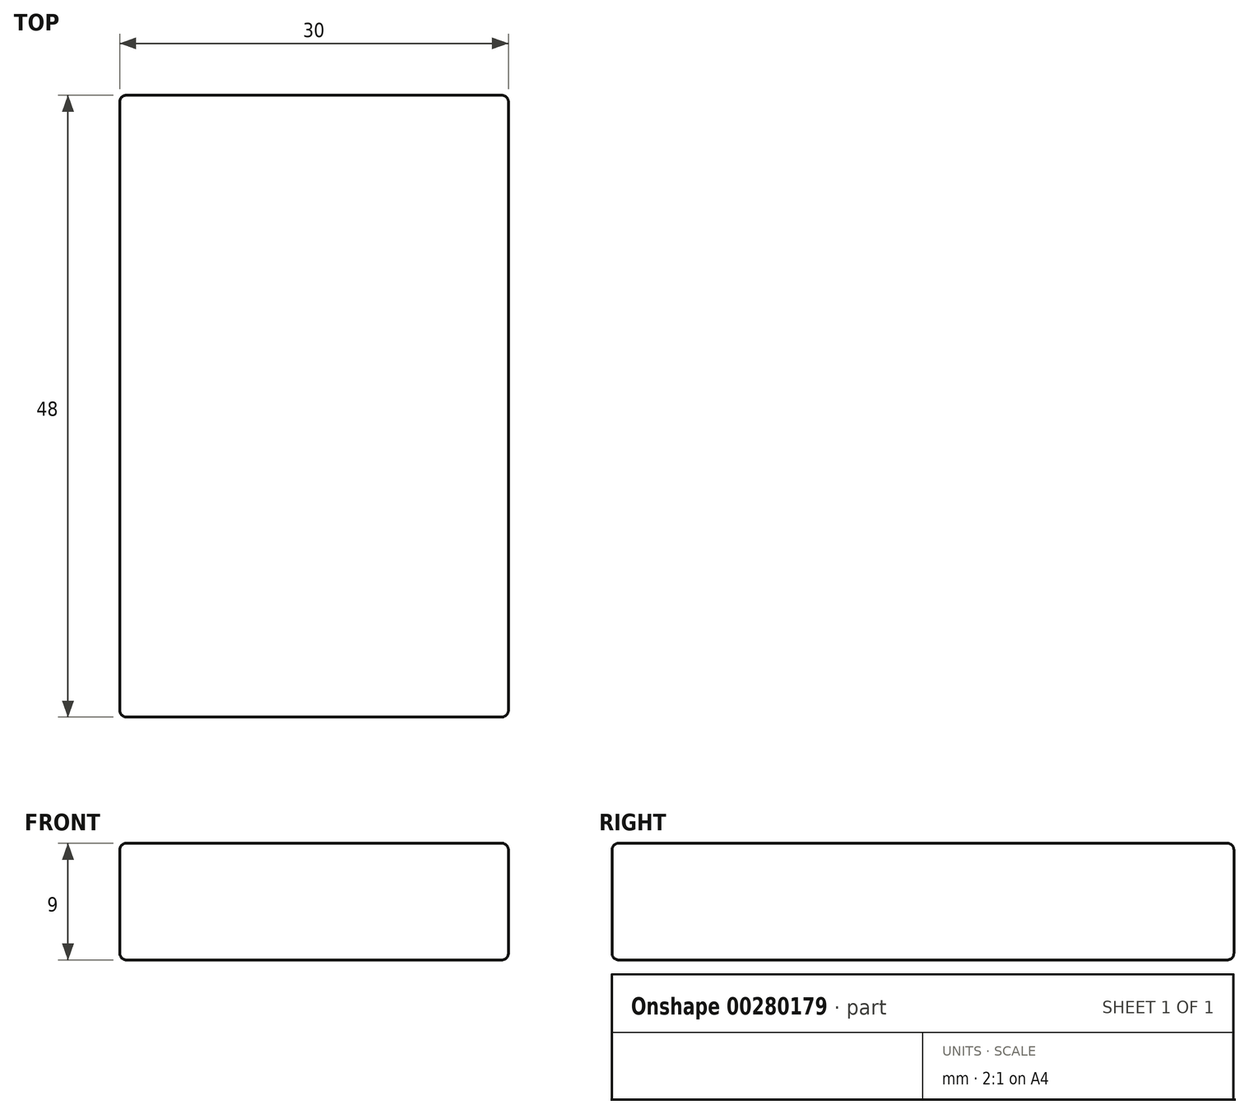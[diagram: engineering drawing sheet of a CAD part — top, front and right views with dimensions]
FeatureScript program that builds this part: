
annotation { "Feature Type Name" : "Feature", "Feature Type Description" : "" }
export const myFeature = defineFeature(function(context is Context, id is Id, definition is map)
    precondition{}
    {
        {
            var Q0;
            Q0=qCreatedBy(makeId("Front.planeOp"),FACE);
            var sketch = newSketch(context, id + "F0", { "sketchPlane" : qUnion([Q0])});
            skLineSegment(sketch, "E0.bottom", {"start": v(15, -4.5) * mm, "end": v(-15, -4.5) * mm});
            skLineSegment(sketch, "E0.top", {"start": v(15, 4.5) * mm, "end": v(-15, 4.5) * mm});
            skLineSegment(sketch, "E0.left", {"start": v(15, -4.5) * mm, "end": v(15, 4.5) * mm});
            skLineSegment(sketch, "E0.right", {"start": v(-15, -4.5) * mm, "end": v(-15, 4.5) * mm});
            skPoint(sketch, "E0.middle", {"position": v(0, 0) * mm});
            skSolve(sketch);
        }
        {
            var Q0;
            Q0 = qSketchRegion(id + "F0", true);
            extrude(context, id + "F1", {"entities" : qUnion([Q0]), "depth" : 48 * mm, "symmetric" : true});
        }
        {
            var Q0;
            Q0=makeQuery(id+"F1.opExtrude","SWEPT_EDGE",EDGE,{"disambiguationData":[OSD([sQuery(id+"F0.wireOp",EDGE,"E0.bottom"),sQuery(id+"F0.wireOp",EDGE,"E0.left")])]});
            var Q1;
            Q1=makeQuery(id+"F1.opExtrude","SWEPT_FACE",FACE,{"disambiguationData":[OSD([sQuery(id+"F0.wireOp",EDGE,"E0.bottom")])]});
            var Q2;
            Q2=makeQuery(id+"F1.opExtrude","CAP_FACE",FACE,{"disambiguationData":[OSD([sQuery(id+"F0.wireOp",EDGE,"E0.bottom"),sQuery(id+"F0.wireOp",EDGE,"E0.top"),sQuery(id+"F0.wireOp",EDGE,"E0.left"),sQuery(id+"F0.wireOp",EDGE,"E0.right")])],"isStart":true});
            var Q3;
            Q3=makeQuery(id+"F1.opExtrude","SWEPT_EDGE",EDGE,{"disambiguationData":[OSD([sQuery(id+"F0.wireOp",EDGE,"E0.top"),sQuery(id+"F0.wireOp",EDGE,"E0.left")])]});
            var Q4;
            Q4=makeQuery(id+"F1.opExtrude","CAP_FACE",FACE,{"disambiguationData":[OSD([sQuery(id+"F0.wireOp",EDGE,"E0.bottom"),sQuery(id+"F0.wireOp",EDGE,"E0.top"),sQuery(id+"F0.wireOp",EDGE,"E0.left"),sQuery(id+"F0.wireOp",EDGE,"E0.right")])],"isStart":false});
            var Q5;
            Q5=makeQuery(id+"F1.opExtrude","SWEPT_EDGE",EDGE,{"disambiguationData":[OSD([sQuery(id+"F0.wireOp",EDGE,"E0.top"),sQuery(id+"F0.wireOp",EDGE,"E0.right")])]});
            var Q6;
            Q6=makeQuery(id+"F1.opExtrude","SWEPT_FACE",FACE,{"disambiguationData":[OSD([sQuery(id+"F0.wireOp",EDGE,"E0.top")])]});
            var Q7;
            Q7=makeQuery(id+"F1.opExtrude","SWEPT_FACE",FACE,{"disambiguationData":[OSD([sQuery(id+"F0.wireOp",EDGE,"E0.left")])]});
            var Q8;
            Q8=makeQuery(id+"F1.opExtrude","SWEPT_EDGE",EDGE,{"disambiguationData":[OSD([sQuery(id+"F0.wireOp",EDGE,"E0.bottom"),sQuery(id+"F0.wireOp",EDGE,"E0.right")])]});
            var Q9;
            Q9=makeQuery(id+"F1.opExtrude","CAP_EDGE",EDGE,{"disambiguationData":[OSD([sQuery(id+"F0.wireOp",EDGE,"E0.bottom")])],"isStart":true});
            var Q10;
            Q10=makeQuery(id+"F1.opExtrude","CAP_EDGE",EDGE,{"disambiguationData":[OSD([sQuery(id+"F0.wireOp",EDGE,"E0.bottom")])],"isStart":false});
            var Q11;
            Q11=makeQuery(id+"F1.opExtrude","SWEPT_FACE",FACE,{"disambiguationData":[OSD([sQuery(id+"F0.wireOp",EDGE,"E0.right")])]});
            var Q12;
            Q12=makeQuery(id+"F1.opExtrude","CAP_EDGE",EDGE,{"disambiguationData":[OSD([sQuery(id+"F0.wireOp",EDGE,"E0.top")])],"isStart":true});
            var Q13;
            Q13=makeQuery(id+"F1.opExtrude","CAP_EDGE",EDGE,{"disambiguationData":[OSD([sQuery(id+"F0.wireOp",EDGE,"E0.top")])],"isStart":false});
            var Q14;
            Q14=makeQuery(id+"F1.opExtrude","CAP_EDGE",EDGE,{"disambiguationData":[OSD([sQuery(id+"F0.wireOp",EDGE,"E0.left")])],"isStart":true});
            var Q15;
            Q15=makeQuery(id+"F1.opExtrude","CAP_EDGE",EDGE,{"disambiguationData":[OSD([sQuery(id+"F0.wireOp",EDGE,"E0.left")])],"isStart":false});
            var Q16;
            Q16=makeQuery(id+"F1.opExtrude","CAP_EDGE",EDGE,{"disambiguationData":[OSD([sQuery(id+"F0.wireOp",EDGE,"E0.right")])],"isStart":true});
            var Q17;
            Q17=makeQuery(id+"F1.opExtrude","CAP_EDGE",EDGE,{"disambiguationData":[OSD([sQuery(id+"F0.wireOp",EDGE,"E0.right")])],"isStart":false});
            fillet(context, id + "F2", {"entities" : qUnion([Q0, Q1, Q2, Q3, Q4, Q5, Q6, Q7, Q8, Q9, Q10, Q11, Q12, Q13, Q14, Q15, Q16, Q17]), "radius" : 0.5 * mm, "tangentPropagation" : true, "allowEdgeOverflow" : false});
        }
    });
